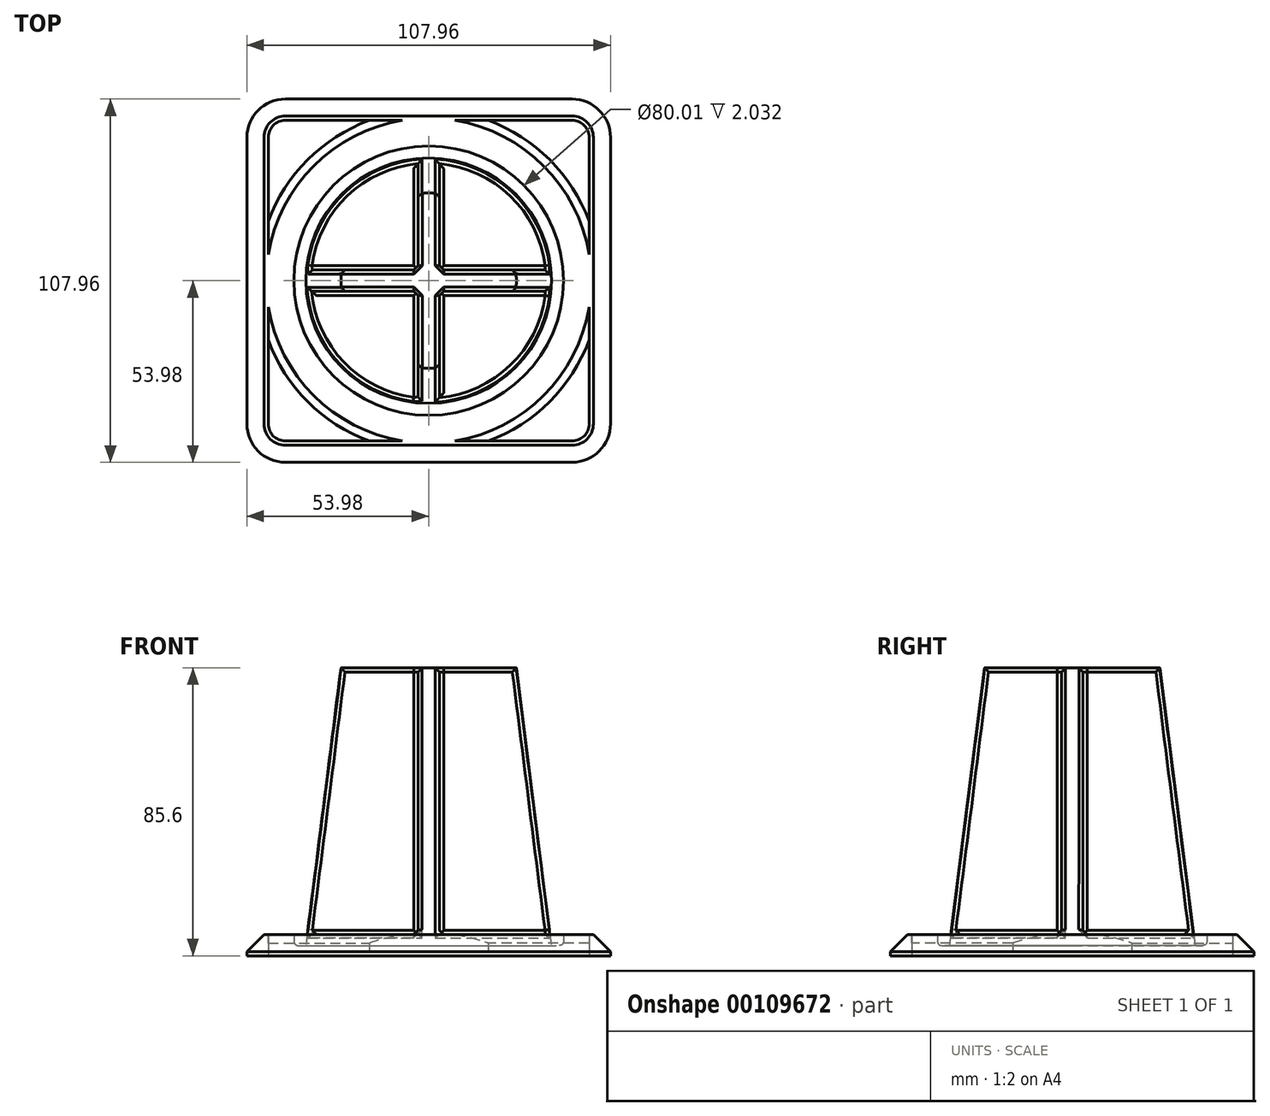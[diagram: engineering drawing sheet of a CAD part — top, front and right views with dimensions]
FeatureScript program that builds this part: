
annotation { "Feature Type Name" : "Feature", "Feature Type Description" : "" }
export const myFeature = defineFeature(function(context is Context, id is Id, definition is map)
    precondition{}
    {
        {
            var Q0;
            Q0=qCreatedBy(makeId("Top.planeOp"),FACE);
            var sketch = newSketch(context, id + "F0", { "sketchPlane" : qUnion([Q0])});
            skCircle(sketch, "E0", {"center": v(0, 0) * mm, "radius": 50.8 * mm});
            skLineSegment(sketch, "E1", {"start": v(0, 75.9) * mm, "end": v(0, -68.67) * mm, "construction": true});
            skLineSegment(sketch, "E2.bottom", {"start": v(-34.93, -25.4) * mm, "end": v(-66.68, -25.4) * mm});
            skLineSegment(sketch, "E2.top", {"start": v(-34.93, 25.4) * mm, "end": v(-66.67, 25.4) * mm});
            skLineSegment(sketch, "E2.left", {"start": v(-34.93, -25.4) * mm, "end": v(-34.93, 25.4) * mm});
            skLineSegment(sketch, "E2.right", {"start": v(-66.67, -25.4) * mm, "end": v(-66.67, 25.4) * mm});
            skPoint(sketch, "E2.middle", {"position": v(-50.8, 0) * mm});
            skLineSegment(sketch, "E3.0", {"start": v(-28.57, 31.75) * mm, "end": v(-73.02, 31.75) * mm});
            skLineSegment(sketch, "E3.1", {"start": v(-28.58, -31.75) * mm, "end": v(-28.57, 31.75) * mm});
            skLineSegment(sketch, "E3.2", {"start": v(-28.58, -31.75) * mm, "end": v(-73.02, -31.75) * mm});
            skLineSegment(sketch, "E3.3", {"start": v(-73.02, -31.75) * mm, "end": v(-73.02, 31.75) * mm});
            skLineSegment(sketch, "E4.MirrorCS", {"start": v(34.93, 25.4) * mm, "end": v(66.68, 25.4) * mm});
            skLineSegment(sketch, "E5.MirrorCS", {"start": v(28.58, 31.75) * mm, "end": v(73.03, 31.75) * mm});
            skLineSegment(sketch, "E6.MirrorCS", {"start": v(73.03, -31.75) * mm, "end": v(73.03, 31.75) * mm});
            skLineSegment(sketch, "E7.MirrorCS", {"start": v(28.58, -31.75) * mm, "end": v(73.03, -31.75) * mm});
            skLineSegment(sketch, "E8.MirrorCS", {"start": v(34.93, -25.4) * mm, "end": v(66.68, -25.4) * mm});
            skLineSegment(sketch, "E9.MirrorCS", {"start": v(28.58, -31.75) * mm, "end": v(28.58, 31.75) * mm});
            skLineSegment(sketch, "E10.MirrorCS", {"start": v(34.93, -25.4) * mm, "end": v(34.93, 25.4) * mm});
            skLineSegment(sketch, "E11.MirrorCS", {"start": v(66.68, -25.4) * mm, "end": v(66.68, 25.4) * mm});
            skSolve(sketch);
        }
        {
            var Q0;
            Q0=qCreatedBy(makeId("Top.planeOp"),FACE);
            var sketch = newSketch(context, id + "F1", { "sketchPlane" : qUnion([Q0])});
            skLineSegment(sketch, "E12.bottom", {"start": v(-47.63, 47.62) * mm, "end": v(47.63, 47.62) * mm});
            skLineSegment(sketch, "E12.top", {"start": v(-47.63, -47.62) * mm, "end": v(47.63, -47.62) * mm});
            skLineSegment(sketch, "E12.left", {"start": v(-47.63, 47.63) * mm, "end": v(-47.63, -47.63) * mm});
            skLineSegment(sketch, "E12.right", {"start": v(47.63, 47.63) * mm, "end": v(47.63, -47.63) * mm});
            skPoint(sketch, "E12.middle", {"position": v(0, 0) * mm});
            skLineSegment(sketch, "E13.0", {"start": v(-53.98, -53.98) * mm, "end": v(53.98, -53.98) * mm});
            skLineSegment(sketch, "E13.1", {"start": v(-53.98, 53.98) * mm, "end": v(-53.98, -53.98) * mm});
            skLineSegment(sketch, "E13.2", {"start": v(-53.98, 53.98) * mm, "end": v(53.98, 53.98) * mm});
            skLineSegment(sketch, "E13.3", {"start": v(53.98, 53.98) * mm, "end": v(53.98, -53.98) * mm});
            skSolve(sketch);
        }
        {
            var Q0;
            {var subQ0=sQuery(id+"F0.wireOp",EDGE,"E3.1");Q0=makeQuery(id+"F0.imprint","IMPRINT",FACE,{"disambiguationData":[TD([[makeQuery(id+"F0.imprint","IMPRINT",EDGE,{"derivedFrom":subQ0}),-1.0]])]});}
            var Q1;
            {var subQ0=sQuery(id+"F0.wireOp",EDGE,"E2.left");Q1=makeQuery(id+"F0.imprint","IMPRINT",FACE,{"disambiguationData":[TD([[makeQuery(id+"F0.imprint","IMPRINT",EDGE,{"derivedFrom":subQ0}),-1.0]])]});}
            var Q2;
            {var subQ5=sQuery(id+"F0.wireOp",EDGE,"E2.left");Q2=makeQuery(id+"F0.imprint","IMPRINT",FACE,{"disambiguationData":[TD([[makeQuery(id+"F0.imprint","IMPRINT",EDGE,{"derivedFrom":subQ5}),1.0]])]});}
            var Q3;
            {var subQ0=sQuery(id+"F0.wireOp",EDGE,"E9.MirrorCS");Q3=makeQuery(id+"F0.imprint","IMPRINT",FACE,{"disambiguationData":[TD([[makeQuery(id+"F0.imprint","IMPRINT",EDGE,{"derivedFrom":subQ0}),-1.0]])]});}
            var Q4;
            {var subQ5=sQuery(id+"F0.wireOp",EDGE,"E10.MirrorCS");Q4=makeQuery(id+"F0.imprint","IMPRINT",FACE,{"disambiguationData":[TD([[makeQuery(id+"F0.imprint","IMPRINT",EDGE,{"derivedFrom":subQ5}),-1.0]])]});}
            extrude(context, id + "F2", {"entities" : qUnion([Q0, Q1, Q2, Q3, Q4]), "depth" : 6.35 * mm});
        }
        {
            var Q0;
            Q0 = qSketchRegion(id + "F1", true);
            extrude(context, id + "F3", {"entities" : qUnion([Q0]), "operationType" : NewBodyOperationType.ADD, "depth" : 6.35 * mm});
        }
        {
            var Q0;
            Q0=qCreatedBy(makeId("Top.planeOp"),FACE);
            cPlane(context, id + "F4", {"entities" : qUnion([Q0]), "cplaneType" : CPlaneType.OFFSET, "offset" : 3.05 * mm, "width" : 152.4 * mm, "height" : 152.4 * mm});
        }
        {
            var Q0;
            Q0=qCreatedBy(id+"F4.planeOp",FACE);
            var sketch = newSketch(context, id + "F5", { "sketchPlane" : qUnion([Q0])});
            skLineSegment(sketch, "E14.bottom", {"start": v(3.18, -50.7) * mm, "end": v(-3.17, -50.7) * mm});
            skLineSegment(sketch, "E14.top", {"start": v(3.17, 50.7) * mm, "end": v(-3.18, 50.7) * mm});
            skLineSegment(sketch, "E14.left", {"start": v(3.18, -50.7) * mm, "end": v(3.18, 50.7) * mm});
            skLineSegment(sketch, "E14.right", {"start": v(-3.18, -50.7) * mm, "end": v(-3.18, 50.7) * mm});
            skPoint(sketch, "E14.middle", {"position": v(0, 0) * mm});
            skLineSegment(sketch, "E15.bottom", {"start": v(50.7, -3.17) * mm, "end": v(-50.7, -3.18) * mm});
            skLineSegment(sketch, "E15.top", {"start": v(50.7, 3.18) * mm, "end": v(-50.7, 3.17) * mm});
            skLineSegment(sketch, "E15.left", {"start": v(50.7, -3.18) * mm, "end": v(50.7, 3.18) * mm});
            skLineSegment(sketch, "E15.right", {"start": v(-50.7, -3.18) * mm, "end": v(-50.7, 3.18) * mm});
            skSolve(sketch);
        }
        {
            var Q0;
            Q0 = qSketchRegion(id + "F5", true);
            extrude(context, id + "F6", {"entities" : qUnion([Q0]), "operationType" : NewBodyOperationType.ADD, "depth" : 82.55 * mm});
        }
        {
            var Q0;
            Q0=qCreatedBy(makeId("Front.planeOp"),FACE);
            var sketch = newSketch(context, id + "F7", { "sketchPlane" : qUnion([Q0])});
            skLineSegment(sketch, "E16", {"start": v(0, 85.6) * mm, "end": v(0, 0) * mm, "construction": true});
            skLineSegment(sketch, "E17", {"start": v(0, 85.6) * mm, "end": v(26.04, 85.6) * mm});
            skLineSegment(sketch, "E18", {"start": v(26.03, 85.6) * mm, "end": v(36.45, 3.05) * mm});
            skLineSegment(sketch, "E19", {"start": v(36.45, 3.05) * mm, "end": v(40, 3.05) * mm});
            skLineSegment(sketch, "E20", {"start": v(40, 3.05) * mm, "end": v(40, 6.35) * mm});
            skLineSegment(sketch, "E21", {"start": v(40, 6.35) * mm, "end": v(64.67, 6.35) * mm});
            skLineSegment(sketch, "E22", {"start": v(64.67, 6.35) * mm, "end": v(64.67, 85.6) * mm});
            skLineSegment(sketch, "E23", {"start": v(64.67, 85.6) * mm, "end": v(26.04, 85.6) * mm});
            skSolve(sketch);
        }
        {
            var Q0;
            Q0=makeQuery(id+"F7.imprint","IMPRINT",FACE,{"disambiguationData":[TD([[makeQuery(id+"F7.imprint","IMPRINT",EDGE,{"derivedFrom":sQuery(id+"F7.wireOp",EDGE,"E18")}),1.0]])]});
            var Q1;
            Q1=sQuery(id+"F7.wireOp",EDGE,"E16");
            revolve(context, id + "F8", {"operationType" : NewBodyOperationType.REMOVE, "entities" : qUnion([Q0]), "axis" : qUnion([Q1]), "revolveType" : RevolveType.FULL, "oppositeDirection" : true});
        }
        {
            var Q0;
            Q0=makeQuery(id+"F8.boolean.opBoolean","COPY",EDGE,{"derivedFrom":makeQuery(id+"F8.opRevolve","SWEPT_EDGE",EDGE,{"disambiguationData":[OSD([sQuery(id+"F7.wireOp",EDGE,"E19"),sQuery(id+"F7.wireOp",EDGE,"E20")])]})});
            fillet(context, id + "F9", {"entities" : qUnion([Q0]), "radius" : 1.27 * mm, "tangentPropagation" : true, "allowEdgeOverflow" : false});
        }
        {
            var Q0;
            {var subQ0=sQuery(id+"F5.wireOp",EDGE,"E14.right");Q0=makeQuery(id+"F8.boolean.opBoolean","INTERSECT",EDGE,{"derivedFrom":[makeQuery(id+"F6.opExtrude","SWEPT_FACE",FACE,{"disambiguationData":[OSD([subQ0]),TDD([makeQuery(id+"F5.imprint","IMPRINT",EDGE,{"disambiguationData":[TD([[makeQuery(id+"F5.imprint","INTERSECT",VERTEX,{"derivedFrom":[sQuery(id+"F5.wireOp",EDGE,"E14.bottom"),subQ0]}),-1.0]])],"derivedFrom":subQ0})])]}),makeQuery(id+"F8.opRevolve","SWEPT_FACE",FACE,{"disambiguationData":[OSD([sQuery(id+"F7.wireOp",EDGE,"E18")])]})]});}
            var Q1;
            {var subQ0=sQuery(id+"F5.wireOp",EDGE,"E14.left");Q1=makeQuery(id+"F8.boolean.opBoolean","INTERSECT",EDGE,{"derivedFrom":[makeQuery(id+"F6.opExtrude","SWEPT_FACE",FACE,{"disambiguationData":[OSD([subQ0]),TDD([makeQuery(id+"F5.imprint","IMPRINT",EDGE,{"disambiguationData":[TD([[makeQuery(id+"F5.imprint","INTERSECT",VERTEX,{"derivedFrom":[sQuery(id+"F5.wireOp",EDGE,"E14.bottom"),subQ0]}),-1.0]])],"derivedFrom":subQ0})])]}),makeQuery(id+"F8.opRevolve","SWEPT_FACE",FACE,{"disambiguationData":[OSD([sQuery(id+"F7.wireOp",EDGE,"E18")])]})]});}
            var Q2;
            {var subQ0=sQuery(id+"F5.wireOp",EDGE,"E15.bottom");Q2=makeQuery(id+"F8.boolean.opBoolean","INTERSECT",EDGE,{"derivedFrom":[makeQuery(id+"F6.opExtrude","SWEPT_FACE",FACE,{"disambiguationData":[OSD([subQ0]),TDD([makeQuery(id+"F5.imprint","IMPRINT",EDGE,{"disambiguationData":[TD([[makeQuery(id+"F5.imprint","INTERSECT",VERTEX,{"derivedFrom":[subQ0,sQuery(id+"F5.wireOp",EDGE,"E15.right")]}),1.0]])],"derivedFrom":subQ0})])]}),makeQuery(id+"F8.opRevolve","SWEPT_FACE",FACE,{"disambiguationData":[OSD([sQuery(id+"F7.wireOp",EDGE,"E18")])]})]});}
            var Q3;
            {var subQ0=sQuery(id+"F5.wireOp",EDGE,"E15.top");Q3=makeQuery(id+"F8.boolean.opBoolean","INTERSECT",EDGE,{"derivedFrom":[makeQuery(id+"F6.opExtrude","SWEPT_FACE",FACE,{"disambiguationData":[OSD([subQ0]),TDD([makeQuery(id+"F5.imprint","IMPRINT",EDGE,{"disambiguationData":[TD([[makeQuery(id+"F5.imprint","INTERSECT",VERTEX,{"derivedFrom":[subQ0,sQuery(id+"F5.wireOp",EDGE,"E15.right")]}),1.0]])],"derivedFrom":subQ0})])]}),makeQuery(id+"F8.opRevolve","SWEPT_FACE",FACE,{"disambiguationData":[OSD([sQuery(id+"F7.wireOp",EDGE,"E18")])]})]});}
            var Q4;
            {var subQ0=sQuery(id+"F5.wireOp",EDGE,"E14.right");Q4=makeQuery(id+"F8.boolean.opBoolean","INTERSECT",EDGE,{"derivedFrom":[makeQuery(id+"F6.opExtrude","SWEPT_FACE",FACE,{"disambiguationData":[OSD([subQ0]),TDD([makeQuery(id+"F5.imprint","IMPRINT",EDGE,{"disambiguationData":[TD([[makeQuery(id+"F5.imprint","INTERSECT",VERTEX,{"derivedFrom":[sQuery(id+"F5.wireOp",EDGE,"E14.top"),subQ0]}),1.0]])],"derivedFrom":subQ0})])]}),makeQuery(id+"F8.opRevolve","SWEPT_FACE",FACE,{"disambiguationData":[OSD([sQuery(id+"F7.wireOp",EDGE,"E18")])]})]});}
            var Q5;
            {var subQ0=sQuery(id+"F5.wireOp",EDGE,"E15.bottom");Q5=makeQuery(id+"F8.boolean.opBoolean","INTERSECT",EDGE,{"derivedFrom":[makeQuery(id+"F6.opExtrude","SWEPT_FACE",FACE,{"disambiguationData":[OSD([subQ0]),TDD([makeQuery(id+"F5.imprint","IMPRINT",EDGE,{"disambiguationData":[TD([[makeQuery(id+"F5.imprint","INTERSECT",VERTEX,{"derivedFrom":[subQ0,sQuery(id+"F5.wireOp",EDGE,"E15.left")]}),-1.0]])],"derivedFrom":subQ0})])]}),makeQuery(id+"F8.opRevolve","SWEPT_FACE",FACE,{"disambiguationData":[OSD([sQuery(id+"F7.wireOp",EDGE,"E18")])]})]});}
            var Q6;
            {var subQ0=sQuery(id+"F5.wireOp",EDGE,"E14.left");Q6=makeQuery(id+"F8.boolean.opBoolean","INTERSECT",EDGE,{"derivedFrom":[makeQuery(id+"F6.opExtrude","SWEPT_FACE",FACE,{"disambiguationData":[OSD([subQ0]),TDD([makeQuery(id+"F5.imprint","IMPRINT",EDGE,{"disambiguationData":[TD([[makeQuery(id+"F5.imprint","INTERSECT",VERTEX,{"derivedFrom":[sQuery(id+"F5.wireOp",EDGE,"E14.top"),subQ0]}),1.0]])],"derivedFrom":subQ0})])]}),makeQuery(id+"F8.opRevolve","SWEPT_FACE",FACE,{"disambiguationData":[OSD([sQuery(id+"F7.wireOp",EDGE,"E18")])]})]});}
            var Q7;
            {var subQ0=sQuery(id+"F5.wireOp",EDGE,"E15.top");Q7=makeQuery(id+"F8.boolean.opBoolean","INTERSECT",EDGE,{"derivedFrom":[makeQuery(id+"F6.opExtrude","SWEPT_FACE",FACE,{"disambiguationData":[OSD([subQ0]),TDD([makeQuery(id+"F5.imprint","IMPRINT",EDGE,{"disambiguationData":[TD([[makeQuery(id+"F5.imprint","INTERSECT",VERTEX,{"derivedFrom":[subQ0,sQuery(id+"F5.wireOp",EDGE,"E15.left")]}),-1.0]])],"derivedFrom":subQ0})])]}),makeQuery(id+"F8.opRevolve","SWEPT_FACE",FACE,{"disambiguationData":[OSD([sQuery(id+"F7.wireOp",EDGE,"E18")])]})]});}
            var Q8;
            {var subQ0=sQuery(id+"F5.wireOp",EDGE,"E15.top");Q8=makeQuery(id+"F6.boolean.opBoolean","INTERSECT",EDGE,{"derivedFrom":[makeQuery(id+"F2.opExtrude","CAP_FACE",FACE,{"disambiguationData":[OSD([sQuery(id+"F0.wireOp",EDGE,"E0"),sQuery(id+"F0.wireOp",EDGE,"E2.bottom"),sQuery(id+"F0.wireOp",EDGE,"E2.top"),sQuery(id+"F0.wireOp",EDGE,"E2.right"),sQuery(id+"F0.wireOp",EDGE,"E3.0"),sQuery(id+"F0.wireOp",EDGE,"E3.2"),sQuery(id+"F0.wireOp",EDGE,"E3.3"),sQuery(id+"F0.wireOp",EDGE,"E4.MirrorCS"),sQuery(id+"F0.wireOp",EDGE,"E5.MirrorCS"),sQuery(id+"F0.wireOp",EDGE,"E6.MirrorCS"),sQuery(id+"F0.wireOp",EDGE,"E7.MirrorCS"),sQuery(id+"F0.wireOp",EDGE,"E8.MirrorCS"),sQuery(id+"F0.wireOp",EDGE,"E11.MirrorCS")])],"isStart":false}),makeQuery(id+"F6.opExtrude","SWEPT_FACE",FACE,{"disambiguationData":[OSD([subQ0]),TDD([makeQuery(id+"F5.imprint","IMPRINT",EDGE,{"disambiguationData":[TD([[makeQuery(id+"F5.imprint","INTERSECT",VERTEX,{"derivedFrom":[subQ0,sQuery(id+"F5.wireOp",EDGE,"E15.right")]}),1.0]])],"derivedFrom":subQ0})])]})]});}
            var Q9;
            {var subQ0=sQuery(id+"F5.wireOp",EDGE,"E14.right");Q9=makeQuery(id+"F6.boolean.opBoolean","INTERSECT",EDGE,{"derivedFrom":[makeQuery(id+"F2.opExtrude","CAP_FACE",FACE,{"disambiguationData":[OSD([sQuery(id+"F0.wireOp",EDGE,"E0"),sQuery(id+"F0.wireOp",EDGE,"E2.bottom"),sQuery(id+"F0.wireOp",EDGE,"E2.top"),sQuery(id+"F0.wireOp",EDGE,"E2.right"),sQuery(id+"F0.wireOp",EDGE,"E3.0"),sQuery(id+"F0.wireOp",EDGE,"E3.2"),sQuery(id+"F0.wireOp",EDGE,"E3.3"),sQuery(id+"F0.wireOp",EDGE,"E4.MirrorCS"),sQuery(id+"F0.wireOp",EDGE,"E5.MirrorCS"),sQuery(id+"F0.wireOp",EDGE,"E6.MirrorCS"),sQuery(id+"F0.wireOp",EDGE,"E7.MirrorCS"),sQuery(id+"F0.wireOp",EDGE,"E8.MirrorCS"),sQuery(id+"F0.wireOp",EDGE,"E11.MirrorCS")])],"isStart":false}),makeQuery(id+"F6.opExtrude","SWEPT_FACE",FACE,{"disambiguationData":[OSD([subQ0]),TDD([makeQuery(id+"F5.imprint","IMPRINT",EDGE,{"disambiguationData":[TD([[makeQuery(id+"F5.imprint","INTERSECT",VERTEX,{"derivedFrom":[sQuery(id+"F5.wireOp",EDGE,"E14.bottom"),subQ0]}),-1.0]])],"derivedFrom":subQ0})])]})]});}
            var Q10;
            {var subQ0=sQuery(id+"F5.wireOp",EDGE,"E15.top");Q10=makeQuery(id+"F6.boolean.opBoolean","INTERSECT",EDGE,{"derivedFrom":[makeQuery(id+"F2.opExtrude","CAP_FACE",FACE,{"disambiguationData":[OSD([sQuery(id+"F0.wireOp",EDGE,"E0"),sQuery(id+"F0.wireOp",EDGE,"E2.bottom"),sQuery(id+"F0.wireOp",EDGE,"E2.top"),sQuery(id+"F0.wireOp",EDGE,"E2.right"),sQuery(id+"F0.wireOp",EDGE,"E3.0"),sQuery(id+"F0.wireOp",EDGE,"E3.2"),sQuery(id+"F0.wireOp",EDGE,"E3.3"),sQuery(id+"F0.wireOp",EDGE,"E4.MirrorCS"),sQuery(id+"F0.wireOp",EDGE,"E5.MirrorCS"),sQuery(id+"F0.wireOp",EDGE,"E6.MirrorCS"),sQuery(id+"F0.wireOp",EDGE,"E7.MirrorCS"),sQuery(id+"F0.wireOp",EDGE,"E8.MirrorCS"),sQuery(id+"F0.wireOp",EDGE,"E11.MirrorCS")])],"isStart":false}),makeQuery(id+"F6.opExtrude","SWEPT_FACE",FACE,{"disambiguationData":[OSD([subQ0]),TDD([makeQuery(id+"F5.imprint","IMPRINT",EDGE,{"disambiguationData":[TD([[makeQuery(id+"F5.imprint","INTERSECT",VERTEX,{"derivedFrom":[subQ0,sQuery(id+"F5.wireOp",EDGE,"E15.left")]}),-1.0]])],"derivedFrom":subQ0})])]})]});}
            var Q11;
            {var subQ0=sQuery(id+"F5.wireOp",EDGE,"E15.bottom");Q11=makeQuery(id+"F6.boolean.opBoolean","INTERSECT",EDGE,{"derivedFrom":[makeQuery(id+"F2.opExtrude","CAP_FACE",FACE,{"disambiguationData":[OSD([sQuery(id+"F0.wireOp",EDGE,"E0"),sQuery(id+"F0.wireOp",EDGE,"E2.bottom"),sQuery(id+"F0.wireOp",EDGE,"E2.top"),sQuery(id+"F0.wireOp",EDGE,"E2.right"),sQuery(id+"F0.wireOp",EDGE,"E3.0"),sQuery(id+"F0.wireOp",EDGE,"E3.2"),sQuery(id+"F0.wireOp",EDGE,"E3.3"),sQuery(id+"F0.wireOp",EDGE,"E4.MirrorCS"),sQuery(id+"F0.wireOp",EDGE,"E5.MirrorCS"),sQuery(id+"F0.wireOp",EDGE,"E6.MirrorCS"),sQuery(id+"F0.wireOp",EDGE,"E7.MirrorCS"),sQuery(id+"F0.wireOp",EDGE,"E8.MirrorCS"),sQuery(id+"F0.wireOp",EDGE,"E11.MirrorCS")])],"isStart":false}),makeQuery(id+"F6.opExtrude","SWEPT_FACE",FACE,{"disambiguationData":[OSD([subQ0]),TDD([makeQuery(id+"F5.imprint","IMPRINT",EDGE,{"disambiguationData":[TD([[makeQuery(id+"F5.imprint","INTERSECT",VERTEX,{"derivedFrom":[subQ0,sQuery(id+"F5.wireOp",EDGE,"E15.left")]}),-1.0]])],"derivedFrom":subQ0})])]})]});}
            chamfer(context, id + "F10", {"entities" : qUnion([Q0, Q1, Q2, Q3, Q4, Q5, Q6, Q7, Q8, Q9, Q10, Q11]), "width" : 1.27 * mm, "tangentPropagation" : true});
        }
        {
            var Q0;
            {var subQ0=sQuery(id+"F5.wireOp",EDGE,"E14.left");Q0=makeQuery(id+"F6.opExtrude","CAP_EDGE",EDGE,{"disambiguationData":[OSD([subQ0]),TDD([makeQuery(id+"F5.imprint","IMPRINT",EDGE,{"disambiguationData":[TD([[makeQuery(id+"F5.imprint","INTERSECT",VERTEX,{"derivedFrom":[sQuery(id+"F5.wireOp",EDGE,"E14.bottom"),subQ0]}),-1.0]])],"derivedFrom":subQ0})])],"isStart":false});}
            var Q1;
            {var subQ0=sQuery(id+"F5.wireOp",EDGE,"E15.top");Q1=makeQuery(id+"F6.opExtrude","CAP_EDGE",EDGE,{"disambiguationData":[OSD([subQ0]),TDD([makeQuery(id+"F5.imprint","IMPRINT",EDGE,{"disambiguationData":[TD([[makeQuery(id+"F5.imprint","INTERSECT",VERTEX,{"derivedFrom":[subQ0,sQuery(id+"F5.wireOp",EDGE,"E15.left")]}),-1.0]])],"derivedFrom":subQ0})])],"isStart":false});}
            var Q2;
            {var subQ0=sQuery(id+"F5.wireOp",EDGE,"E14.right");Q2=makeQuery(id+"F6.opExtrude","CAP_EDGE",EDGE,{"disambiguationData":[OSD([subQ0]),TDD([makeQuery(id+"F5.imprint","IMPRINT",EDGE,{"disambiguationData":[TD([[makeQuery(id+"F5.imprint","INTERSECT",VERTEX,{"derivedFrom":[sQuery(id+"F5.wireOp",EDGE,"E14.top"),subQ0]}),1.0]])],"derivedFrom":subQ0})])],"isStart":false});}
            var Q3;
            {var subQ0=sQuery(id+"F5.wireOp",EDGE,"E15.bottom");Q3=makeQuery(id+"F6.opExtrude","CAP_EDGE",EDGE,{"disambiguationData":[OSD([subQ0]),TDD([makeQuery(id+"F5.imprint","IMPRINT",EDGE,{"disambiguationData":[TD([[makeQuery(id+"F5.imprint","INTERSECT",VERTEX,{"derivedFrom":[subQ0,sQuery(id+"F5.wireOp",EDGE,"E15.right")]}),1.0]])],"derivedFrom":subQ0})])],"isStart":false});}
            var Q4;
            {var subQ0=sQuery(id+"F5.wireOp",EDGE,"E14.right");Q4=makeQuery(id+"F6.opExtrude","CAP_EDGE",EDGE,{"disambiguationData":[OSD([subQ0]),TDD([makeQuery(id+"F5.imprint","IMPRINT",EDGE,{"disambiguationData":[TD([[makeQuery(id+"F5.imprint","INTERSECT",VERTEX,{"derivedFrom":[sQuery(id+"F5.wireOp",EDGE,"E14.bottom"),subQ0]}),-1.0]])],"derivedFrom":subQ0})])],"isStart":false});}
            var Q5;
            {var subQ0=sQuery(id+"F5.wireOp",EDGE,"E15.top");Q5=makeQuery(id+"F6.opExtrude","CAP_EDGE",EDGE,{"disambiguationData":[OSD([subQ0]),TDD([makeQuery(id+"F5.imprint","IMPRINT",EDGE,{"disambiguationData":[TD([[makeQuery(id+"F5.imprint","INTERSECT",VERTEX,{"derivedFrom":[subQ0,sQuery(id+"F5.wireOp",EDGE,"E15.right")]}),1.0]])],"derivedFrom":subQ0})])],"isStart":false});}
            var Q6;
            {var subQ0=sQuery(id+"F5.wireOp",EDGE,"E14.left");Q6=makeQuery(id+"F6.opExtrude","CAP_EDGE",EDGE,{"disambiguationData":[OSD([subQ0]),TDD([makeQuery(id+"F5.imprint","IMPRINT",EDGE,{"disambiguationData":[TD([[makeQuery(id+"F5.imprint","INTERSECT",VERTEX,{"derivedFrom":[sQuery(id+"F5.wireOp",EDGE,"E14.top"),subQ0]}),1.0]])],"derivedFrom":subQ0})])],"isStart":false});}
            var Q7;
            {var subQ0=sQuery(id+"F5.wireOp",EDGE,"E15.bottom");Q7=makeQuery(id+"F6.opExtrude","CAP_EDGE",EDGE,{"disambiguationData":[OSD([subQ0]),TDD([makeQuery(id+"F5.imprint","IMPRINT",EDGE,{"disambiguationData":[TD([[makeQuery(id+"F5.imprint","INTERSECT",VERTEX,{"derivedFrom":[subQ0,sQuery(id+"F5.wireOp",EDGE,"E15.left")]}),-1.0]])],"derivedFrom":subQ0})])],"isStart":false});}
            var Q8;
            {var subQ0=sQuery(id+"F5.wireOp",EDGE,"E14.left");Q8=makeQuery(id+"F6.boolean.opBoolean","INTERSECT",EDGE,{"derivedFrom":[makeQuery(id+"F2.opExtrude","CAP_FACE",FACE,{"disambiguationData":[OSD([sQuery(id+"F0.wireOp",EDGE,"E0"),sQuery(id+"F0.wireOp",EDGE,"E2.bottom"),sQuery(id+"F0.wireOp",EDGE,"E2.top"),sQuery(id+"F0.wireOp",EDGE,"E2.right"),sQuery(id+"F0.wireOp",EDGE,"E3.0"),sQuery(id+"F0.wireOp",EDGE,"E3.2"),sQuery(id+"F0.wireOp",EDGE,"E3.3"),sQuery(id+"F0.wireOp",EDGE,"E4.MirrorCS"),sQuery(id+"F0.wireOp",EDGE,"E5.MirrorCS"),sQuery(id+"F0.wireOp",EDGE,"E6.MirrorCS"),sQuery(id+"F0.wireOp",EDGE,"E7.MirrorCS"),sQuery(id+"F0.wireOp",EDGE,"E8.MirrorCS"),sQuery(id+"F0.wireOp",EDGE,"E11.MirrorCS")])],"isStart":false}),makeQuery(id+"F6.opExtrude","SWEPT_FACE",FACE,{"disambiguationData":[OSD([subQ0]),TDD([makeQuery(id+"F5.imprint","IMPRINT",EDGE,{"disambiguationData":[TD([[makeQuery(id+"F5.imprint","INTERSECT",VERTEX,{"derivedFrom":[sQuery(id+"F5.wireOp",EDGE,"E14.bottom"),subQ0]}),-1.0]])],"derivedFrom":subQ0})])]})]});}
            var Q9;
            {var subQ0=sQuery(id+"F5.wireOp",EDGE,"E14.left");Q9=makeQuery(id+"F6.boolean.opBoolean","INTERSECT",EDGE,{"derivedFrom":[makeQuery(id+"F2.opExtrude","CAP_FACE",FACE,{"disambiguationData":[OSD([sQuery(id+"F0.wireOp",EDGE,"E0"),sQuery(id+"F0.wireOp",EDGE,"E2.bottom"),sQuery(id+"F0.wireOp",EDGE,"E2.top"),sQuery(id+"F0.wireOp",EDGE,"E2.right"),sQuery(id+"F0.wireOp",EDGE,"E3.0"),sQuery(id+"F0.wireOp",EDGE,"E3.2"),sQuery(id+"F0.wireOp",EDGE,"E3.3"),sQuery(id+"F0.wireOp",EDGE,"E4.MirrorCS"),sQuery(id+"F0.wireOp",EDGE,"E5.MirrorCS"),sQuery(id+"F0.wireOp",EDGE,"E6.MirrorCS"),sQuery(id+"F0.wireOp",EDGE,"E7.MirrorCS"),sQuery(id+"F0.wireOp",EDGE,"E8.MirrorCS"),sQuery(id+"F0.wireOp",EDGE,"E11.MirrorCS")])],"isStart":false}),makeQuery(id+"F6.opExtrude","SWEPT_FACE",FACE,{"disambiguationData":[OSD([subQ0]),TDD([makeQuery(id+"F5.imprint","IMPRINT",EDGE,{"disambiguationData":[TD([[makeQuery(id+"F5.imprint","INTERSECT",VERTEX,{"derivedFrom":[sQuery(id+"F5.wireOp",EDGE,"E14.top"),subQ0]}),1.0]])],"derivedFrom":subQ0})])]})]});}
            var Q10;
            {var subQ0=sQuery(id+"F5.wireOp",EDGE,"E14.right");Q10=makeQuery(id+"F6.boolean.opBoolean","INTERSECT",EDGE,{"derivedFrom":[makeQuery(id+"F2.opExtrude","CAP_FACE",FACE,{"disambiguationData":[OSD([sQuery(id+"F0.wireOp",EDGE,"E0"),sQuery(id+"F0.wireOp",EDGE,"E2.bottom"),sQuery(id+"F0.wireOp",EDGE,"E2.top"),sQuery(id+"F0.wireOp",EDGE,"E2.right"),sQuery(id+"F0.wireOp",EDGE,"E3.0"),sQuery(id+"F0.wireOp",EDGE,"E3.2"),sQuery(id+"F0.wireOp",EDGE,"E3.3"),sQuery(id+"F0.wireOp",EDGE,"E4.MirrorCS"),sQuery(id+"F0.wireOp",EDGE,"E5.MirrorCS"),sQuery(id+"F0.wireOp",EDGE,"E6.MirrorCS"),sQuery(id+"F0.wireOp",EDGE,"E7.MirrorCS"),sQuery(id+"F0.wireOp",EDGE,"E8.MirrorCS"),sQuery(id+"F0.wireOp",EDGE,"E11.MirrorCS")])],"isStart":false}),makeQuery(id+"F6.opExtrude","SWEPT_FACE",FACE,{"disambiguationData":[OSD([subQ0]),TDD([makeQuery(id+"F5.imprint","IMPRINT",EDGE,{"disambiguationData":[TD([[makeQuery(id+"F5.imprint","INTERSECT",VERTEX,{"derivedFrom":[sQuery(id+"F5.wireOp",EDGE,"E14.top"),subQ0]}),1.0]])],"derivedFrom":subQ0})])]})]});}
            var Q11;
            {var subQ0=sQuery(id+"F5.wireOp",EDGE,"E15.bottom");Q11=makeQuery(id+"F6.boolean.opBoolean","INTERSECT",EDGE,{"derivedFrom":[makeQuery(id+"F2.opExtrude","CAP_FACE",FACE,{"disambiguationData":[OSD([sQuery(id+"F0.wireOp",EDGE,"E0"),sQuery(id+"F0.wireOp",EDGE,"E2.bottom"),sQuery(id+"F0.wireOp",EDGE,"E2.top"),sQuery(id+"F0.wireOp",EDGE,"E2.right"),sQuery(id+"F0.wireOp",EDGE,"E3.0"),sQuery(id+"F0.wireOp",EDGE,"E3.2"),sQuery(id+"F0.wireOp",EDGE,"E3.3"),sQuery(id+"F0.wireOp",EDGE,"E4.MirrorCS"),sQuery(id+"F0.wireOp",EDGE,"E5.MirrorCS"),sQuery(id+"F0.wireOp",EDGE,"E6.MirrorCS"),sQuery(id+"F0.wireOp",EDGE,"E7.MirrorCS"),sQuery(id+"F0.wireOp",EDGE,"E8.MirrorCS"),sQuery(id+"F0.wireOp",EDGE,"E11.MirrorCS")])],"isStart":false}),makeQuery(id+"F6.opExtrude","SWEPT_FACE",FACE,{"disambiguationData":[OSD([subQ0]),TDD([makeQuery(id+"F5.imprint","IMPRINT",EDGE,{"disambiguationData":[TD([[makeQuery(id+"F5.imprint","INTERSECT",VERTEX,{"derivedFrom":[subQ0,sQuery(id+"F5.wireOp",EDGE,"E15.right")]}),1.0]])],"derivedFrom":subQ0})])]})]});}
            var Q12;
            Q12=makeQuery(id+"F6.opExtrude","SWEPT_EDGE",EDGE,{"disambiguationData":[OSD([sQuery(id+"F5.wireOp",EDGE,"E14.left"),sQuery(id+"F5.wireOp",EDGE,"E15.bottom")])]});
            var Q13;
            Q13=makeQuery(id+"F6.opExtrude","SWEPT_EDGE",EDGE,{"disambiguationData":[OSD([sQuery(id+"F5.wireOp",EDGE,"E14.left"),sQuery(id+"F5.wireOp",EDGE,"E15.top")])]});
            var Q14;
            Q14=makeQuery(id+"F6.opExtrude","SWEPT_EDGE",EDGE,{"disambiguationData":[OSD([sQuery(id+"F5.wireOp",EDGE,"E14.right"),sQuery(id+"F5.wireOp",EDGE,"E15.top")])]});
            var Q15;
            Q15=makeQuery(id+"F6.opExtrude","SWEPT_EDGE",EDGE,{"disambiguationData":[OSD([sQuery(id+"F5.wireOp",EDGE,"E14.right"),sQuery(id+"F5.wireOp",EDGE,"E15.bottom")])]});
            var Q16;
            Q16=makeQuery(id+"F8.boolean.opBoolean","COPY",EDGE,{"disambiguationData":[OD(2.0)],"derivedFrom":makeQuery(id+"F8.opRevolve","SWEPT_EDGE",EDGE,{"disambiguationData":[OSD([sQuery(id+"F7.wireOp",EDGE,"E18"),sQuery(id+"F7.wireOp",EDGE,"E23")])]})});
            var Q17;
            Q17=makeQuery(id+"F8.boolean.opBoolean","COPY",EDGE,{"disambiguationData":[OD(1.0)],"derivedFrom":makeQuery(id+"F8.opRevolve","SWEPT_EDGE",EDGE,{"disambiguationData":[OSD([sQuery(id+"F7.wireOp",EDGE,"E18"),sQuery(id+"F7.wireOp",EDGE,"E23")])]})});
            var Q18;
            Q18=makeQuery(id+"F8.boolean.opBoolean","COPY",EDGE,{"disambiguationData":[OD(0.0)],"derivedFrom":makeQuery(id+"F8.opRevolve","SWEPT_EDGE",EDGE,{"disambiguationData":[OSD([sQuery(id+"F7.wireOp",EDGE,"E18"),sQuery(id+"F7.wireOp",EDGE,"E23")])]})});
            var Q19;
            Q19=makeQuery(id+"F8.boolean.opBoolean","COPY",EDGE,{"disambiguationData":[OD(3.0)],"derivedFrom":makeQuery(id+"F8.opRevolve","SWEPT_EDGE",EDGE,{"disambiguationData":[OSD([sQuery(id+"F7.wireOp",EDGE,"E18"),sQuery(id+"F7.wireOp",EDGE,"E23")])]})});
            chamfer(context, id + "F11", {"entities" : qUnion([Q0, Q1, Q2, Q3, Q4, Q5, Q6, Q7, Q8, Q9, Q10, Q11, Q12, Q13, Q14, Q15, Q16, Q17, Q18, Q19]), "width" : 1.27 * mm, "tangentPropagation" : true});
        }
        {
            var Q0;
            Q0=makeQuery(id+"F3.opExtrude","SWEPT_EDGE",EDGE,{"disambiguationData":[OSD([sQuery(id+"F1.wireOp",EDGE,"E13.2"),sQuery(id+"F1.wireOp",EDGE,"E13.3")])]});
            var Q1;
            Q1=makeQuery(id+"F3.opExtrude","SWEPT_EDGE",EDGE,{"disambiguationData":[OSD([sQuery(id+"F1.wireOp",EDGE,"E13.0"),sQuery(id+"F1.wireOp",EDGE,"E13.3")])]});
            var Q2;
            Q2=makeQuery(id+"F3.opExtrude","SWEPT_EDGE",EDGE,{"disambiguationData":[OSD([sQuery(id+"F1.wireOp",EDGE,"E13.0"),sQuery(id+"F1.wireOp",EDGE,"E13.1")])]});
            var Q3;
            Q3=makeQuery(id+"F3.opExtrude","SWEPT_EDGE",EDGE,{"disambiguationData":[OSD([sQuery(id+"F1.wireOp",EDGE,"E13.1"),sQuery(id+"F1.wireOp",EDGE,"E13.2")])]});
            fillet(context, id + "F12", {"entities" : qUnion([Q0, Q1, Q2, Q3]), "radius" : 11.43 * mm, "tangentPropagation" : true, "allowEdgeOverflow" : false});
        }
        {
            var Q0;
            Q0=makeQuery(id+"F3.opExtrude","SWEPT_EDGE",EDGE,{"disambiguationData":[OSD([sQuery(id+"F1.wireOp",EDGE,"E12.top"),sQuery(id+"F1.wireOp",EDGE,"E12.left")])]});
            var Q1;
            Q1=makeQuery(id+"F3.opExtrude","SWEPT_EDGE",EDGE,{"disambiguationData":[OSD([sQuery(id+"F1.wireOp",EDGE,"E12.top"),sQuery(id+"F1.wireOp",EDGE,"E12.right")])]});
            var Q2;
            Q2=makeQuery(id+"F3.opExtrude","SWEPT_EDGE",EDGE,{"disambiguationData":[OSD([sQuery(id+"F1.wireOp",EDGE,"E12.bottom"),sQuery(id+"F1.wireOp",EDGE,"E12.right")])]});
            var Q3;
            Q3=makeQuery(id+"F3.opExtrude","SWEPT_EDGE",EDGE,{"disambiguationData":[OSD([sQuery(id+"F1.wireOp",EDGE,"E12.bottom"),sQuery(id+"F1.wireOp",EDGE,"E12.left")])]});
            fillet(context, id + "F13", {"entities" : qUnion([Q0, Q1, Q2, Q3]), "radius" : 5.08 * mm, "tangentPropagation" : true, "allowEdgeOverflow" : false});
        }
        {
            var Q0;
            Q0=makeQuery(id+"F3.opExtrude","CAP_EDGE",EDGE,{"disambiguationData":[OSD([sQuery(id+"F1.wireOp",EDGE,"E13.3")])],"isStart":false});
            var Q1;
            Q1=makeQuery(id+"F3.opExtrude","CAP_EDGE",EDGE,{"disambiguationData":[OSD([sQuery(id+"F1.wireOp",EDGE,"E13.0")])],"isStart":false});
            var Q2;
            Q2=makeQuery(id+"F3.opExtrude","CAP_EDGE",EDGE,{"disambiguationData":[OSD([sQuery(id+"F1.wireOp",EDGE,"E13.2")])],"isStart":false});
            var Q3;
            Q3=makeQuery(id+"F3.opExtrude","CAP_EDGE",EDGE,{"disambiguationData":[OSD([sQuery(id+"F1.wireOp",EDGE,"E13.1")])],"isStart":false});
            chamfer(context, id + "F14", {"entities" : qUnion([Q0, Q1, Q2, Q3]), "width" : 5.08 * mm, "tangentPropagation" : true});
        }
        {
            var Q0;
            {var subQ0=sQuery(id+"F1.wireOp",EDGE,"E12.right");var subQ1=sQuery(id+"F1.wireOp",EDGE,"E12.bottom");var subQ2=sQuery(id+"F0.wireOp",EDGE,"E0");Q0=makeQuery(id+"F3.boolean.opBoolean","SPLIT",EDGE,{"disambiguationData":[TD([makeQuery(id+"F2.opExtrude","SWEPT_FACE",FACE,{"disambiguationData":[OSD([subQ2])]}),makeQuery(id+"F2.opExtrude","CAP_FACE",FACE,{"disambiguationData":[OSD([subQ2])],"isStart":false}),makeQuery(id+"F3.opExtrude","SWEPT_FACE",FACE,{"disambiguationData":[OSD([subQ1])]}),makeQuery(id+"F3.opExtrude","CAP_FACE",FACE,{"disambiguationData":[OSD([subQ1,sQuery(id+"F1.wireOp",EDGE,"E12.top"),sQuery(id+"F1.wireOp",EDGE,"E12.left"),subQ0,sQuery(id+"F1.wireOp",EDGE,"E13.0"),sQuery(id+"F1.wireOp",EDGE,"E13.1"),sQuery(id+"F1.wireOp",EDGE,"E13.2"),sQuery(id+"F1.wireOp",EDGE,"E13.3")])],"isStart":false}),makeQuery(id+"F3.opExtrude","SWEPT_FACE",FACE,{"disambiguationData":[OSD([subQ0])]})])],"derivedFrom":makeQuery(id+"F2.opExtrude","CAP_EDGE",EDGE,{"disambiguationData":[OSD([subQ2])],"isStart":false})});}
            var Q1;
            {var subQ0=sQuery(id+"F1.wireOp",EDGE,"E12.top");var subQ1=sQuery(id+"F1.wireOp",EDGE,"E12.right");var subQ2=sQuery(id+"F0.wireOp",EDGE,"E0");Q1=makeQuery(id+"F3.boolean.opBoolean","SPLIT",EDGE,{"disambiguationData":[TD([makeQuery(id+"F2.opExtrude","SWEPT_FACE",FACE,{"disambiguationData":[OSD([subQ2])]}),makeQuery(id+"F2.opExtrude","CAP_FACE",FACE,{"disambiguationData":[OSD([subQ2])],"isStart":false}),makeQuery(id+"F3.opExtrude","CAP_FACE",FACE,{"disambiguationData":[OSD([sQuery(id+"F1.wireOp",EDGE,"E12.bottom"),subQ0,sQuery(id+"F1.wireOp",EDGE,"E12.left"),subQ1,sQuery(id+"F1.wireOp",EDGE,"E13.0"),sQuery(id+"F1.wireOp",EDGE,"E13.1"),sQuery(id+"F1.wireOp",EDGE,"E13.2"),sQuery(id+"F1.wireOp",EDGE,"E13.3")])],"isStart":false}),makeQuery(id+"F3.opExtrude","SWEPT_FACE",FACE,{"disambiguationData":[OSD([subQ0])]}),makeQuery(id+"F3.opExtrude","SWEPT_FACE",FACE,{"disambiguationData":[OSD([subQ1])]})])],"derivedFrom":makeQuery(id+"F2.opExtrude","CAP_EDGE",EDGE,{"disambiguationData":[OSD([subQ2])],"isStart":false})});}
            var Q2;
            {var subQ0=sQuery(id+"F1.wireOp",EDGE,"E12.top");var subQ1=sQuery(id+"F1.wireOp",EDGE,"E12.left");var subQ2=sQuery(id+"F0.wireOp",EDGE,"E0");Q2=makeQuery(id+"F3.boolean.opBoolean","SPLIT",EDGE,{"disambiguationData":[TD([makeQuery(id+"F2.opExtrude","SWEPT_FACE",FACE,{"disambiguationData":[OSD([subQ2])]}),makeQuery(id+"F2.opExtrude","CAP_FACE",FACE,{"disambiguationData":[OSD([subQ2])],"isStart":false}),makeQuery(id+"F3.opExtrude","CAP_FACE",FACE,{"disambiguationData":[OSD([sQuery(id+"F1.wireOp",EDGE,"E12.bottom"),subQ0,subQ1,sQuery(id+"F1.wireOp",EDGE,"E12.right"),sQuery(id+"F1.wireOp",EDGE,"E13.0"),sQuery(id+"F1.wireOp",EDGE,"E13.1"),sQuery(id+"F1.wireOp",EDGE,"E13.2"),sQuery(id+"F1.wireOp",EDGE,"E13.3")])],"isStart":false}),makeQuery(id+"F3.opExtrude","SWEPT_FACE",FACE,{"disambiguationData":[OSD([subQ0])]}),makeQuery(id+"F3.opExtrude","SWEPT_FACE",FACE,{"disambiguationData":[OSD([subQ1])]})])],"derivedFrom":makeQuery(id+"F2.opExtrude","CAP_EDGE",EDGE,{"disambiguationData":[OSD([subQ2])],"isStart":false})});}
            var Q3;
            {var subQ0=sQuery(id+"F1.wireOp",EDGE,"E12.left");var subQ1=sQuery(id+"F1.wireOp",EDGE,"E12.bottom");var subQ2=sQuery(id+"F0.wireOp",EDGE,"E0");Q3=makeQuery(id+"F3.boolean.opBoolean","SPLIT",EDGE,{"disambiguationData":[TD([makeQuery(id+"F2.opExtrude","SWEPT_FACE",FACE,{"disambiguationData":[OSD([subQ2])]}),makeQuery(id+"F2.opExtrude","CAP_FACE",FACE,{"disambiguationData":[OSD([subQ2])],"isStart":false}),makeQuery(id+"F3.opExtrude","SWEPT_FACE",FACE,{"disambiguationData":[OSD([subQ1])]}),makeQuery(id+"F3.opExtrude","CAP_FACE",FACE,{"disambiguationData":[OSD([subQ1,sQuery(id+"F1.wireOp",EDGE,"E12.top"),subQ0,sQuery(id+"F1.wireOp",EDGE,"E12.right"),sQuery(id+"F1.wireOp",EDGE,"E13.0"),sQuery(id+"F1.wireOp",EDGE,"E13.1"),sQuery(id+"F1.wireOp",EDGE,"E13.2"),sQuery(id+"F1.wireOp",EDGE,"E13.3")])],"isStart":false}),makeQuery(id+"F3.opExtrude","SWEPT_FACE",FACE,{"disambiguationData":[OSD([subQ0])]})])],"derivedFrom":makeQuery(id+"F2.opExtrude","CAP_EDGE",EDGE,{"disambiguationData":[OSD([subQ2])],"isStart":false})});}
            chamfer(context, id + "F15", {"entities" : qUnion([Q0, Q1, Q2, Q3]), "width" : 2.54 * mm, "tangentPropagation" : true});
        }
    });
